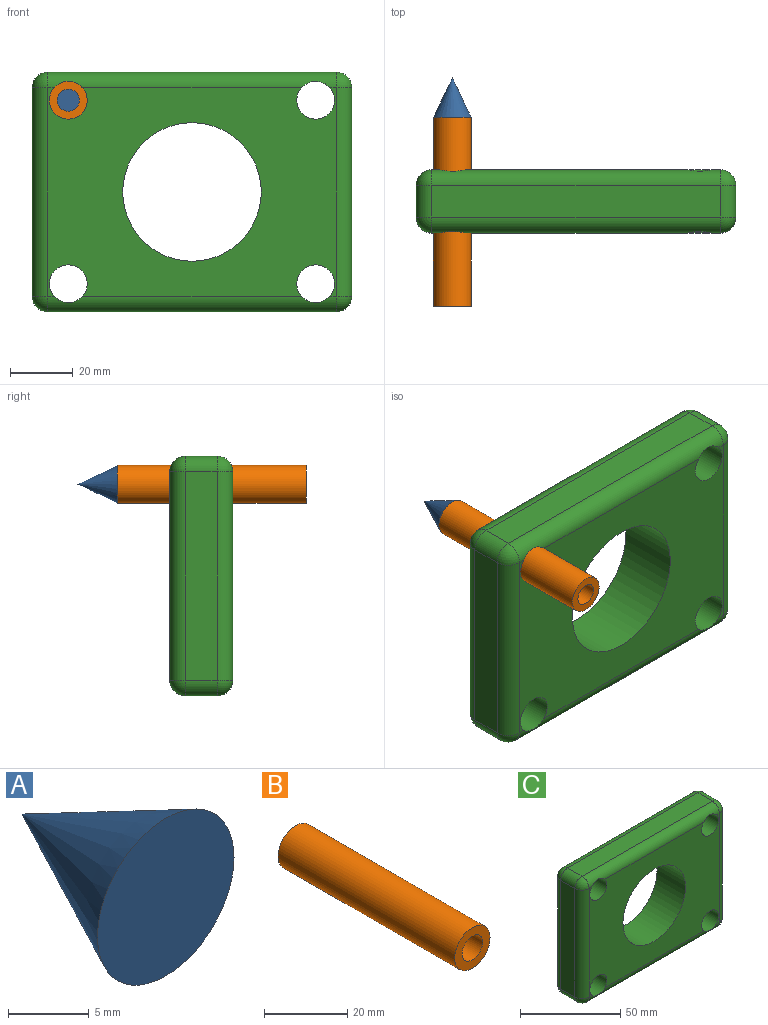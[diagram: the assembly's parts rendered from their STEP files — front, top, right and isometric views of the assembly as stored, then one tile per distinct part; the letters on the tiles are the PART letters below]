
ASSEMBLY  parts=3 mates=2
PART A: 2 faces, bbox 11.9x12.6x11.9 mm
  f0: cone r=0mm half-angle=25.4deg, axis (0,-1,0), area 261.4mm2, adj f1
  f1: plane 11.95x11.95mm, normal (0,-1,0), area 112.1mm2, adj f0
PART B: 4 faces, bbox 12x60x12 mm
  f0: cylinder r=3.5mm len=60mm, axis (0,1,0), area 1319.5mm2, adj f2,f3
  f1: cylinder r=6mm len=60mm, axis (0,1,0), area 2261.9mm2, adj f2,f3
  f2: plane 12x12mm, normal (0,-1,0), area 74.6mm2, adj f0,f1
  f3: plane 12x12mm, normal (0,1,0), area 74.6mm2, adj f0,f1
PART C: 31 faces, bbox 101.6x20x76.2 mm
  f0: plane 91.6x10mm, normal (0,0,-1), area 916mm2, adj f19,f24,f27,f30
  f1: plane 66.2x10mm, normal (1,0,0), area 662mm2, adj f16,f25,f26,f30
  f2: plane 91.6x10mm, normal (0,0,1), area 916mm2, adj f11,f15,f16,f17
  f3: cylinder r=22mm len=44mm, axis (0,1,0), area 2764.6mm2, adj f9,f10
  f4: cylinder r=6mm len=20mm, axis (0,1,0), area 749.3mm2, adj f9,f10,f15,f17
  f5: cylinder r=6mm len=20mm, axis (0,1,0), area 749.3mm2, adj f9,f10,f24,f27
  f6: cylinder r=6mm len=20mm, axis (0,1,0), area 749.3mm2, adj f9,f10,f24,f27
  f7: cylinder r=6mm len=20mm, axis (0,1,0), area 749.3mm2, adj f9,f10,f15,f17
  f8: plane 66.2x10mm, normal (-1,0,0), area 662mm2, adj f11,f14,f18,f19
  f9: plane 91.6x66.2mm, normal (0,-1,0), area 4142.4mm2, adj f3,f4,f5,f6,f7,f14,f15,f24
  f10: plane 91.6x66.2mm, normal (0,1,0), area 4142.4mm2, adj f3,f4,f5,f6,f7,f17,f18,f26
  f11: cylinder r=5mm len=10mm, axis (0,-1,0), area 78.5mm2, adj f2,f8,f12,f13
  f12: sphere r=5mm, area 39.3mm2, adj f11,f14,f15
  f13: sphere r=5mm, area 39.3mm2, adj f11,f17,f18
  f14: cylinder r=5mm len=66.2mm, axis (0,0,1), area 519.9mm2, adj f8,f9,f12,f20
  f15: cylinder r=5mm len=91.6mm, axis (1,0,0), area 693.2mm2, adj f2,f4,f7,f9,f12,f21
  f16: cylinder r=5mm len=10mm, axis (0,1,0), area 78.5mm2, adj f1,f2,f21,f22
  f17: cylinder r=5mm len=91.6mm, axis (-1,0,0), area 693.2mm2, adj f2,f4,f7,f10,f13,f22
  f18: cylinder r=5mm len=66.2mm, axis (0,0,-1), area 519.9mm2, adj f8,f10,f13,f23
  f19: cylinder r=5mm len=10mm, axis (0,1,0), area 78.5mm2, adj f0,f8,f20,f23
  f20: sphere r=5mm, area 39.3mm2, adj f14,f19,f24
  f21: sphere r=5mm, area 39.3mm2, adj f15,f16,f25
  f22: sphere r=5mm, area 39.3mm2, adj f16,f17,f26
  f23: sphere r=5mm, area 39.3mm2, adj f18,f19,f27
  f24: cylinder r=5mm len=91.6mm, axis (-1,0,0), area 693.2mm2, adj f0,f5,f6,f9,f20,f28
  f25: cylinder r=5mm len=66.2mm, axis (0,0,-1), area 519.9mm2, adj f1,f9,f21,f28
  f26: cylinder r=5mm len=66.2mm, axis (0,0,1), area 519.9mm2, adj f1,f10,f22,f29
  f27: cylinder r=5mm len=91.6mm, axis (1,0,0), area 693.2mm2, adj f0,f5,f6,f10,f23,f29
  f28: sphere r=5mm, area 39.3mm2, adj f24,f25,f30
  f29: sphere r=5mm, area 39.3mm2, adj f26,f27,f30
  f30: cylinder r=5mm len=10mm, axis (0,-1,0), area 78.5mm2, adj f0,f1,f28,f29
PLACE A t=(-24.23,-3.33,27.09)mm
PLACE B t=(-24.23,-3.32,27.09)mm
PLACE C t=(15.07,0,-2.06)mm
MATE slider B.f1 <-> C.f4  axis (0,1,0) through (-24.23,-3.32,27.09)mm
MATE fastened A.f0 <-> B.f1  axis (0,-1,0) through (-24.23,26.68,27.09)mm
